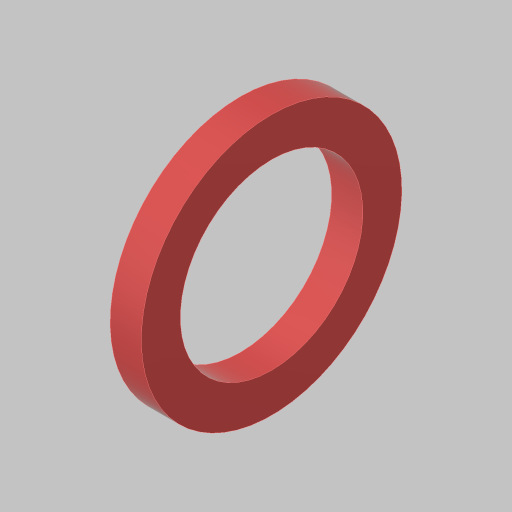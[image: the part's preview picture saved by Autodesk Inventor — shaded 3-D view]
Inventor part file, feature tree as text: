
AUTODESK INVENTOR PART (.ipt)
format: ipt  version: 2023.5 (Build 275446000, 446)  size: 107,008 bytes
history: native  units: in
note: dims shown in document units (in); Inventor stores cm internally (conversion verified against a paired STEP export)
features: extrude x1, sketch x1
ambient origin geometry x8: Origin, YZ Plane, XZ Plane, XY Plane, X Axis, Y Axis, Z Axis, Center Point
bodies: Solid1 (feature_tree)
feature tree (2):
  extrude  "Extrusion1"  Depth=0.1in
  sketch  "Sketch1"  dims[d0=0.585in d1=0.125in d2=0.1in d3=0.0in]
